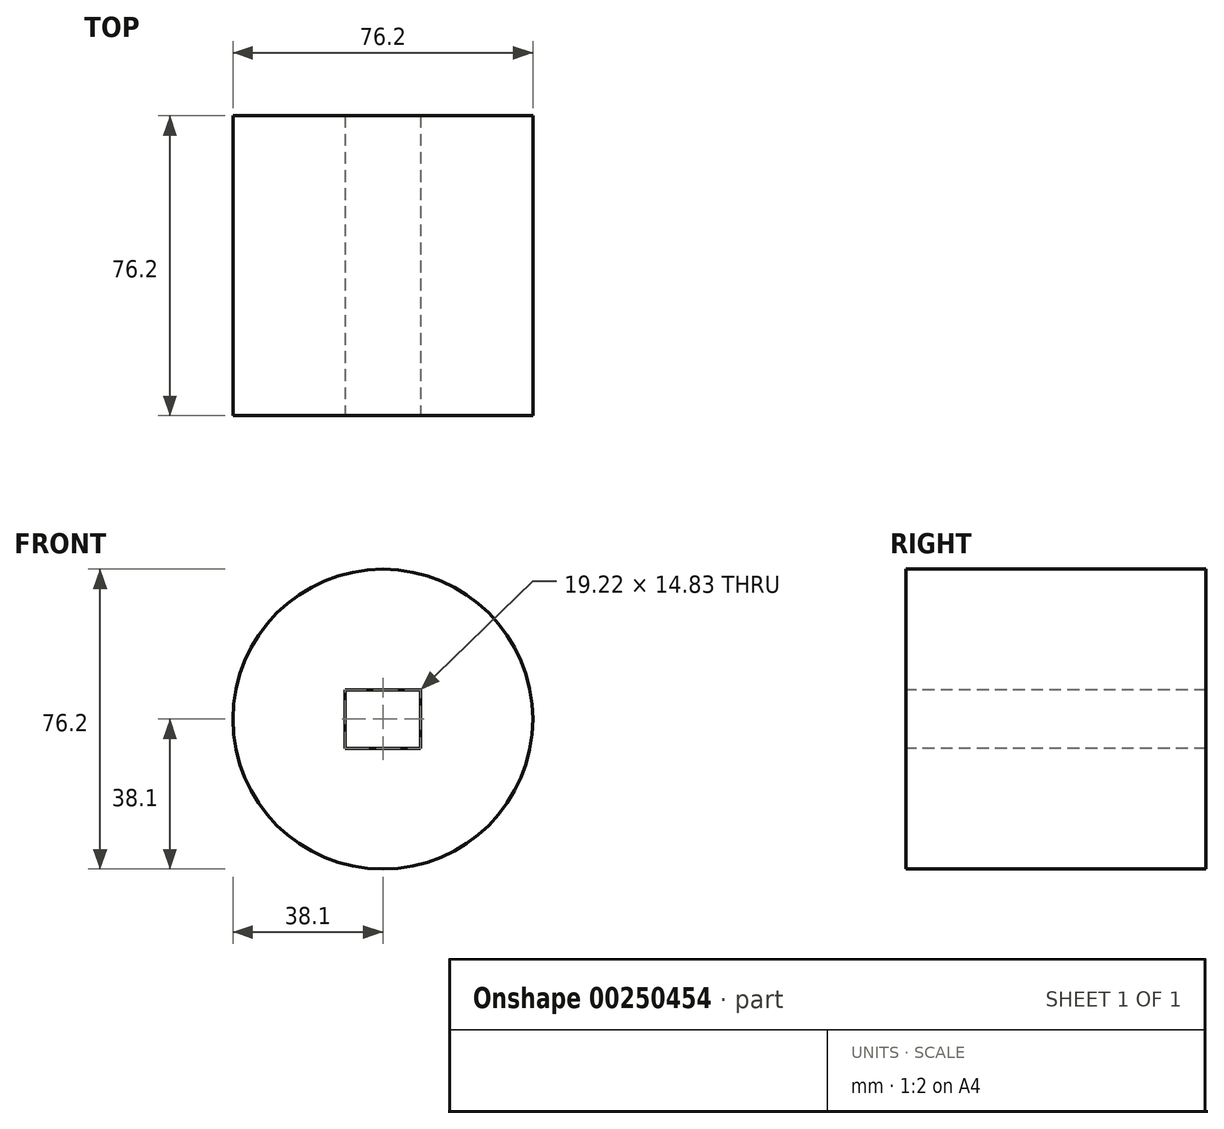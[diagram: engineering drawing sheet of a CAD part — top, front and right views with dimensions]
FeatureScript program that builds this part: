
annotation { "Feature Type Name" : "Feature", "Feature Type Description" : "" }
export const myFeature = defineFeature(function(context is Context, id is Id, definition is map)
    precondition{}
    {
        {
            var Q0;
            Q0=qCreatedBy(makeId("Front.planeOp"),FACE);
            var sketch = newSketch(context, id + "F0", { "sketchPlane" : qUnion([Q0])});
            skCircle(sketch, "E0", {"center": v(0, 0) * mm, "radius": 38.1 * mm});
            skSolve(sketch);
        }
        {
            var Q0;
            Q0=makeQuery(id+"F0.imprint","IMPRINT",FACE,{"disambiguationData":[TD([[makeQuery(id+"F0.imprint","IMPRINT",EDGE,{"derivedFrom":sQuery(id+"F0.wireOp",EDGE,"E0")}),1.0]])]});
            extrude(context, id + "F1", {"entities" : qUnion([Q0]), "depth" : 76.2 * mm});
        }
        {
            var Q0;
            Q0=makeQuery(id+"F1.opExtrude","CAP_FACE",FACE,{"disambiguationData":[OSD([sQuery(id+"F0.wireOp",EDGE,"E0")])],"isStart":false});
            var sketch = newSketch(context, id + "F2", { "sketchPlane" : qUnion([Q0])});
            skLineSegment(sketch, "E1.left", {"start": v(0, -2.2) * mm, "end": v(0, 2.2) * mm});
            skLineSegment(sketch, "E2.bottom", {"start": v(-9.61, 7.42) * mm, "end": v(9.61, 7.42) * mm});
            skLineSegment(sketch, "E2.top", {"start": v(-9.61, -7.42) * mm, "end": v(9.61, -7.42) * mm});
            skLineSegment(sketch, "E2.left", {"start": v(-9.61, 7.42) * mm, "end": v(-9.61, -7.42) * mm});
            skLineSegment(sketch, "E2.right", {"start": v(9.61, 7.42) * mm, "end": v(9.61, -7.42) * mm});
            skPoint(sketch, "E2.middle", {"position": v(0, 0) * mm});
            skSolve(sketch);
        }
        {
            var Q0;
            Q0=makeQuery(id+"F2.imprint","IMPRINT",FACE,{"disambiguationData":[TD([[makeQuery(id+"F2.imprint","IMPRINT",EDGE,{"derivedFrom":sQuery(id+"F2.wireOp",EDGE,"E2.bottom")}),-1.0]])]});
            extrude(context, id + "F3", {"entities" : qUnion([Q0]), "operationType" : NewBodyOperationType.REMOVE, "endBound" : BoundingType.THROUGH_ALL, "oppositeDirection" : true, "depth" : 25.4 * mm});
        }
    });
